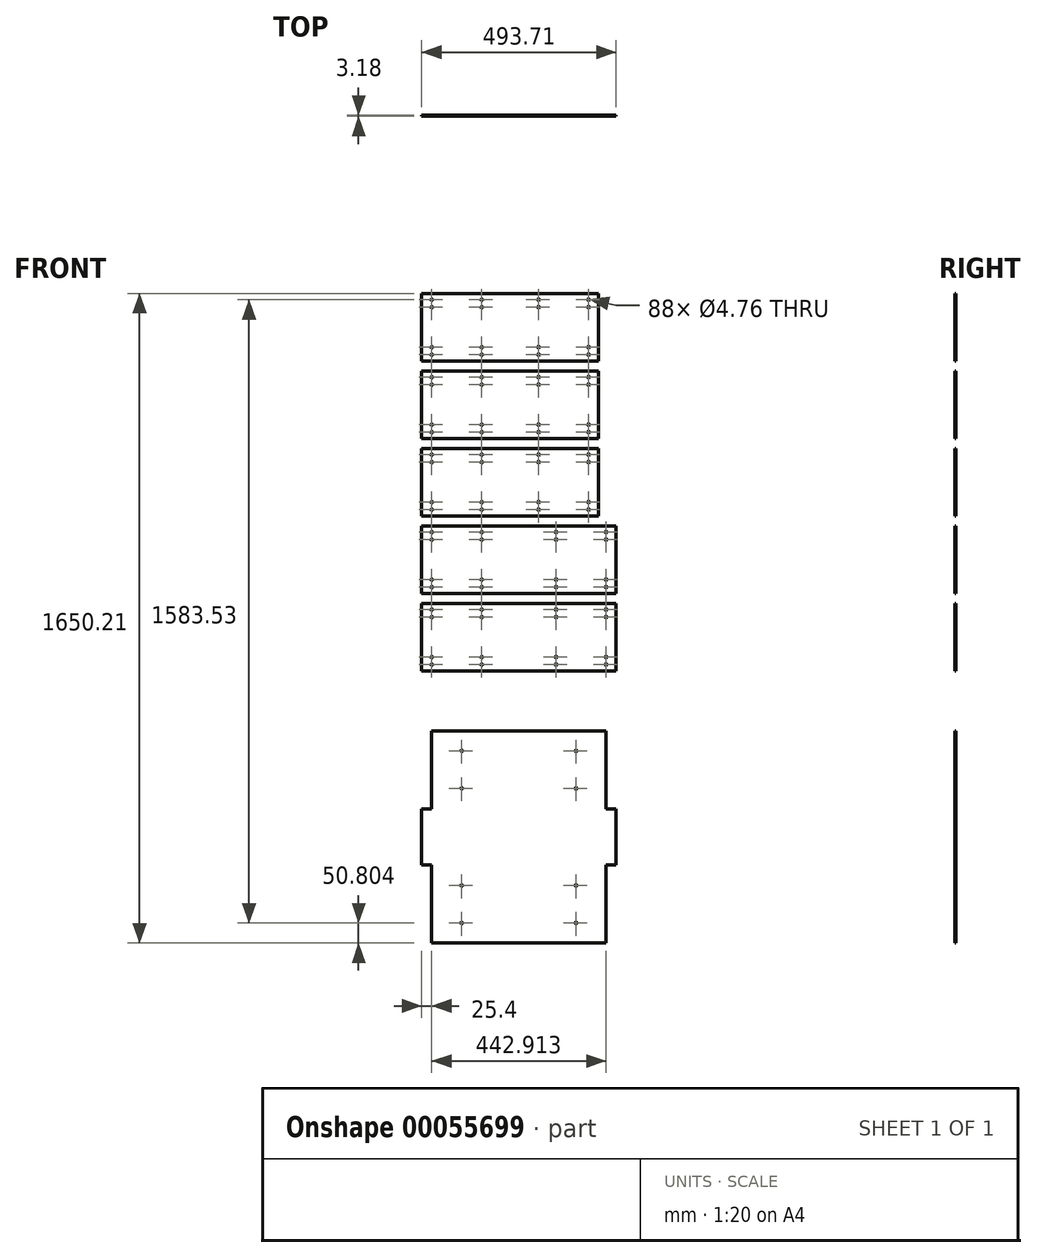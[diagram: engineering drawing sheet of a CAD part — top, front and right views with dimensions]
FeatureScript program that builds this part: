
annotation { "Feature Type Name" : "Feature", "Feature Type Description" : "" }
export const myFeature = defineFeature(function(context is Context, id is Id, definition is map)
    precondition{}
    {
        {
            var Q0;
            Q0=qCreatedBy(makeId("Front.planeOp"),FACE);
            var sketch = newSketch(context, id + "F0", { "sketchPlane" : qUnion([Q0])});
            skLineSegment(sketch, "E0", {"start": v(0, 0) * mm, "end": v(0, -2201.05) * mm, "construction": true});
            skLineSegment(sketch, "E1.bottom", {"start": v(0, 0) * mm, "end": v(449.26, 0) * mm});
            skLineSegment(sketch, "E1.top", {"start": v(0, -171.45) * mm, "end": v(449.26, -171.45) * mm});
            skLineSegment(sketch, "E1.left", {"start": v(0, 0) * mm, "end": v(0, -171.45) * mm});
            skLineSegment(sketch, "E1.right", {"start": v(449.26, 0) * mm, "end": v(449.26, -171.45) * mm});
            skLineSegment(sketch, "E2", {"start": v(0, -15.88) * mm, "end": v(449.26, -15.88) * mm, "construction": true});
            skLineSegment(sketch, "E3", {"start": v(0, -34.93) * mm, "end": v(449.26, -34.93) * mm, "construction": true});
            skLineSegment(sketch, "E4", {"start": v(0, -136.53) * mm, "end": v(449.26, -136.52) * mm, "construction": true});
            skLineSegment(sketch, "E5", {"start": v(0, -155.58) * mm, "end": v(449.26, -155.58) * mm, "construction": true});
            skCircle(sketch, "E6", {"center": v(25.4, -15.88) * mm, "radius": 2.38 * mm});
            skCircle(sketch, "E7", {"center": v(152.4, -15.88) * mm, "radius": 2.38 * mm});
            skCircle(sketch, "E8", {"center": v(296.86, -15.87) * mm, "radius": 2.38 * mm});
            skCircle(sketch, "E9", {"center": v(423.86, -15.87) * mm, "radius": 2.38 * mm});
            skCircle(sketch, "E10", {"center": v(25.4, -34.93) * mm, "radius": 2.38 * mm});
            skCircle(sketch, "E11", {"center": v(152.4, -34.93) * mm, "radius": 2.38 * mm});
            skCircle(sketch, "E12", {"center": v(296.86, -34.92) * mm, "radius": 2.38 * mm});
            skCircle(sketch, "E13", {"center": v(423.86, -34.92) * mm, "radius": 2.38 * mm});
            skCircle(sketch, "E14", {"center": v(25.4, -136.53) * mm, "radius": 2.38 * mm});
            skCircle(sketch, "E15", {"center": v(152.4, -136.53) * mm, "radius": 2.38 * mm});
            skCircle(sketch, "E16", {"center": v(296.86, -136.52) * mm, "radius": 2.38 * mm});
            skCircle(sketch, "E17", {"center": v(423.86, -136.52) * mm, "radius": 2.38 * mm});
            skCircle(sketch, "E18", {"center": v(25.4, -155.58) * mm, "radius": 2.38 * mm});
            skCircle(sketch, "E19", {"center": v(152.4, -155.58) * mm, "radius": 2.38 * mm});
            skCircle(sketch, "E20", {"center": v(296.86, -155.57) * mm, "radius": 2.38 * mm});
            skCircle(sketch, "E21", {"center": v(423.86, -155.57) * mm, "radius": 2.38 * mm});
            skLineSegment(sketch, "E22", {"start": v(25.4, -15.88) * mm, "end": v(25.4, -155.58) * mm, "construction": true});
            skLineSegment(sketch, "E23", {"start": v(152.4, -15.88) * mm, "end": v(152.4, -155.58) * mm, "construction": true});
            skLineSegment(sketch, "E24", {"start": v(296.86, -15.87) * mm, "end": v(296.86, -155.57) * mm, "construction": true});
            skLineSegment(sketch, "E25", {"start": v(423.86, -15.87) * mm, "end": v(423.86, -155.57) * mm, "construction": true});
            skLineSegment(sketch, "E26.bottom", {"start": v(0, -590.55) * mm, "end": v(493.71, -590.55) * mm});
            skLineSegment(sketch, "E26.top", {"start": v(0, -762) * mm, "end": v(493.71, -762) * mm});
            skLineSegment(sketch, "E26.left", {"start": v(0, -590.55) * mm, "end": v(0, -762) * mm});
            skLineSegment(sketch, "E26.right", {"start": v(493.71, -590.55) * mm, "end": v(493.71, -762) * mm});
            skLineSegment(sketch, "E27", {"start": v(0, -606.43) * mm, "end": v(493.71, -606.43) * mm, "construction": true});
            skLineSegment(sketch, "E28", {"start": v(0, -727.08) * mm, "end": v(493.71, -727.08) * mm, "construction": true});
            skLineSegment(sketch, "E29", {"start": v(0, -625.48) * mm, "end": v(493.71, -625.48) * mm, "construction": true});
            skLineSegment(sketch, "E30", {"start": v(0, -746.13) * mm, "end": v(493.71, -746.13) * mm, "construction": true});
            skLineSegment(sketch, "E31", {"start": v(25.4, -590.55) * mm, "end": v(25.4, -762) * mm, "construction": true});
            skLineSegment(sketch, "E32", {"start": v(152.4, -590.55) * mm, "end": v(152.4, -762) * mm, "construction": true});
            skLineSegment(sketch, "E33", {"start": v(341.31, -590.55) * mm, "end": v(341.31, -762) * mm, "construction": true});
            skLineSegment(sketch, "E34", {"start": v(468.31, -590.55) * mm, "end": v(468.31, -762) * mm, "construction": true});
            skCircle(sketch, "E35", {"center": v(25.4, -606.43) * mm, "radius": 2.38 * mm});
            skCircle(sketch, "E36", {"center": v(25.4, -625.48) * mm, "radius": 2.38 * mm});
            skCircle(sketch, "E37", {"center": v(152.4, -606.43) * mm, "radius": 2.38 * mm});
            skCircle(sketch, "E38", {"center": v(152.4, -625.48) * mm, "radius": 2.38 * mm});
            skCircle(sketch, "E39", {"center": v(341.31, -606.43) * mm, "radius": 2.38 * mm});
            skCircle(sketch, "E40", {"center": v(468.31, -606.43) * mm, "radius": 2.38 * mm});
            skCircle(sketch, "E41", {"center": v(468.31, -625.48) * mm, "radius": 2.38 * mm});
            skCircle(sketch, "E42", {"center": v(341.31, -625.48) * mm, "radius": 2.38 * mm});
            skCircle(sketch, "E43", {"center": v(25.4, -727.08) * mm, "radius": 2.38 * mm});
            skCircle(sketch, "E44", {"center": v(25.4, -746.13) * mm, "radius": 2.38 * mm});
            skCircle(sketch, "E45", {"center": v(152.4, -746.13) * mm, "radius": 2.38 * mm});
            skCircle(sketch, "E46", {"center": v(152.4, -727.08) * mm, "radius": 2.38 * mm});
            skCircle(sketch, "E47", {"center": v(341.31, -727.08) * mm, "radius": 2.38 * mm});
            skCircle(sketch, "E48", {"center": v(341.31, -746.13) * mm, "radius": 2.38 * mm});
            skCircle(sketch, "E49", {"center": v(468.31, -727.08) * mm, "radius": 2.38 * mm});
            skCircle(sketch, "E50", {"center": v(468.31, -746.13) * mm, "radius": 2.38 * mm});
            skLineSegment(sketch, "E51.bottom", {"start": v(0, -196.85) * mm, "end": v(449.26, -196.85) * mm});
            skLineSegment(sketch, "E51.top", {"start": v(0, -368.3) * mm, "end": v(449.26, -368.3) * mm});
            skLineSegment(sketch, "E51.left", {"start": v(0, -196.85) * mm, "end": v(0, -368.3) * mm});
            skLineSegment(sketch, "E51.right", {"start": v(449.26, -196.85) * mm, "end": v(449.26, -368.3) * mm});
            skLineSegment(sketch, "E52", {"start": v(0, -212.73) * mm, "end": v(449.26, -212.72) * mm, "construction": true});
            skLineSegment(sketch, "E53", {"start": v(0, -231.78) * mm, "end": v(449.26, -231.77) * mm, "construction": true});
            skLineSegment(sketch, "E54", {"start": v(0, -333.38) * mm, "end": v(449.26, -333.37) * mm, "construction": true});
            skLineSegment(sketch, "E55", {"start": v(0, -352.43) * mm, "end": v(449.26, -352.43) * mm, "construction": true});
            skCircle(sketch, "E56", {"center": v(25.4, -212.73) * mm, "radius": 2.38 * mm});
            skCircle(sketch, "E57", {"center": v(152.4, -212.73) * mm, "radius": 2.38 * mm});
            skCircle(sketch, "E58", {"center": v(296.86, -212.72) * mm, "radius": 2.38 * mm});
            skCircle(sketch, "E59", {"center": v(423.86, -212.72) * mm, "radius": 2.38 * mm});
            skCircle(sketch, "E60", {"center": v(25.4, -231.78) * mm, "radius": 2.38 * mm});
            skCircle(sketch, "E61", {"center": v(152.4, -231.78) * mm, "radius": 2.38 * mm});
            skCircle(sketch, "E62", {"center": v(296.86, -231.77) * mm, "radius": 2.38 * mm});
            skCircle(sketch, "E63", {"center": v(423.86, -231.77) * mm, "radius": 2.38 * mm});
            skCircle(sketch, "E64", {"center": v(25.4, -333.38) * mm, "radius": 2.38 * mm});
            skCircle(sketch, "E65", {"center": v(152.4, -333.38) * mm, "radius": 2.38 * mm});
            skCircle(sketch, "E66", {"center": v(296.86, -333.38) * mm, "radius": 2.38 * mm});
            skCircle(sketch, "E67", {"center": v(423.86, -333.37) * mm, "radius": 2.38 * mm});
            skCircle(sketch, "E68", {"center": v(25.4, -352.43) * mm, "radius": 2.38 * mm});
            skCircle(sketch, "E69", {"center": v(152.4, -352.43) * mm, "radius": 2.38 * mm});
            skCircle(sketch, "E70", {"center": v(296.86, -352.43) * mm, "radius": 2.38 * mm});
            skCircle(sketch, "E71", {"center": v(423.86, -352.43) * mm, "radius": 2.38 * mm});
            skLineSegment(sketch, "E72", {"start": v(25.4, -212.73) * mm, "end": v(25.4, -352.43) * mm, "construction": true});
            skLineSegment(sketch, "E73", {"start": v(152.4, -212.73) * mm, "end": v(152.4, -352.43) * mm, "construction": true});
            skLineSegment(sketch, "E74", {"start": v(296.86, -212.72) * mm, "end": v(296.86, -352.43) * mm, "construction": true});
            skLineSegment(sketch, "E75", {"start": v(423.86, -212.72) * mm, "end": v(423.86, -352.43) * mm, "construction": true});
            skLineSegment(sketch, "E76.bottom", {"start": v(0, -393.7) * mm, "end": v(449.26, -393.7) * mm});
            skLineSegment(sketch, "E76.top", {"start": v(0, -565.15) * mm, "end": v(449.26, -565.15) * mm});
            skLineSegment(sketch, "E76.left", {"start": v(0, -393.7) * mm, "end": v(0, -565.15) * mm});
            skLineSegment(sketch, "E76.right", {"start": v(449.26, -393.7) * mm, "end": v(449.26, -565.15) * mm});
            skLineSegment(sketch, "E77", {"start": v(0, -409.58) * mm, "end": v(449.26, -409.57) * mm, "construction": true});
            skLineSegment(sketch, "E78", {"start": v(0, -428.63) * mm, "end": v(449.26, -428.62) * mm, "construction": true});
            skLineSegment(sketch, "E79", {"start": v(0, -530.23) * mm, "end": v(449.26, -530.22) * mm, "construction": true});
            skLineSegment(sketch, "E80", {"start": v(0, -549.28) * mm, "end": v(449.26, -549.28) * mm, "construction": true});
            skCircle(sketch, "E81", {"center": v(25.4, -409.58) * mm, "radius": 2.38 * mm});
            skCircle(sketch, "E82", {"center": v(152.4, -409.58) * mm, "radius": 2.38 * mm});
            skCircle(sketch, "E83", {"center": v(296.86, -409.58) * mm, "radius": 2.38 * mm});
            skCircle(sketch, "E84", {"center": v(423.86, -409.57) * mm, "radius": 2.38 * mm});
            skCircle(sketch, "E85", {"center": v(25.4, -428.63) * mm, "radius": 2.38 * mm});
            skCircle(sketch, "E86", {"center": v(152.4, -428.63) * mm, "radius": 2.38 * mm});
            skCircle(sketch, "E87", {"center": v(296.86, -428.63) * mm, "radius": 2.38 * mm});
            skCircle(sketch, "E88", {"center": v(423.86, -428.62) * mm, "radius": 2.38 * mm});
            skCircle(sketch, "E89", {"center": v(25.4, -530.23) * mm, "radius": 2.38 * mm});
            skCircle(sketch, "E90", {"center": v(152.4, -530.23) * mm, "radius": 2.38 * mm});
            skCircle(sketch, "E91", {"center": v(296.86, -530.23) * mm, "radius": 2.38 * mm});
            skCircle(sketch, "E92", {"center": v(423.86, -530.22) * mm, "radius": 2.38 * mm});
            skCircle(sketch, "E93", {"center": v(25.4, -549.28) * mm, "radius": 2.38 * mm});
            skCircle(sketch, "E94", {"center": v(152.4, -549.28) * mm, "radius": 2.38 * mm});
            skCircle(sketch, "E95", {"center": v(296.86, -549.28) * mm, "radius": 2.38 * mm});
            skCircle(sketch, "E96", {"center": v(423.86, -549.28) * mm, "radius": 2.38 * mm});
            skLineSegment(sketch, "E97", {"start": v(25.4, -409.58) * mm, "end": v(25.4, -549.28) * mm, "construction": true});
            skLineSegment(sketch, "E98", {"start": v(152.4, -409.58) * mm, "end": v(152.4, -549.28) * mm, "construction": true});
            skLineSegment(sketch, "E99", {"start": v(296.86, -409.58) * mm, "end": v(296.86, -549.28) * mm, "construction": true});
            skLineSegment(sketch, "E100", {"start": v(423.86, -409.57) * mm, "end": v(423.86, -549.28) * mm, "construction": true});
            skLineSegment(sketch, "E101.bottom", {"start": v(0, -787.4) * mm, "end": v(493.71, -787.4) * mm});
            skLineSegment(sketch, "E101.top", {"start": v(0, -958.85) * mm, "end": v(493.71, -958.85) * mm});
            skLineSegment(sketch, "E101.left", {"start": v(0, -787.4) * mm, "end": v(0, -958.85) * mm});
            skLineSegment(sketch, "E101.right", {"start": v(493.71, -787.4) * mm, "end": v(493.71, -958.85) * mm});
            skLineSegment(sketch, "E102", {"start": v(0, -803.28) * mm, "end": v(493.71, -803.28) * mm, "construction": true});
            skLineSegment(sketch, "E103", {"start": v(0, -923.93) * mm, "end": v(493.71, -923.92) * mm, "construction": true});
            skLineSegment(sketch, "E104", {"start": v(0, -822.33) * mm, "end": v(493.71, -822.33) * mm, "construction": true});
            skLineSegment(sketch, "E105", {"start": v(0, -942.98) * mm, "end": v(493.71, -942.98) * mm, "construction": true});
            skLineSegment(sketch, "E106", {"start": v(25.4, -787.4) * mm, "end": v(25.4, -958.85) * mm, "construction": true});
            skLineSegment(sketch, "E107", {"start": v(152.4, -787.4) * mm, "end": v(152.4, -958.85) * mm, "construction": true});
            skLineSegment(sketch, "E108", {"start": v(341.31, -787.4) * mm, "end": v(341.31, -958.85) * mm, "construction": true});
            skLineSegment(sketch, "E109", {"start": v(468.31, -787.4) * mm, "end": v(468.31, -958.85) * mm, "construction": true});
            skCircle(sketch, "E110", {"center": v(25.4, -803.28) * mm, "radius": 2.38 * mm});
            skCircle(sketch, "E111", {"center": v(25.4, -822.33) * mm, "radius": 2.38 * mm});
            skCircle(sketch, "E112", {"center": v(152.4, -803.28) * mm, "radius": 2.38 * mm});
            skCircle(sketch, "E113", {"center": v(152.4, -822.33) * mm, "radius": 2.38 * mm});
            skCircle(sketch, "E114", {"center": v(468.31, -822.33) * mm, "radius": 2.38 * mm});
            skCircle(sketch, "E115", {"center": v(152.4, -942.98) * mm, "radius": 2.38 * mm});
            skCircle(sketch, "E116", {"center": v(152.4, -923.93) * mm, "radius": 2.38 * mm});
            skCircle(sketch, "E117", {"center": v(341.31, -942.98) * mm, "radius": 2.38 * mm});
            skCircle(sketch, "E118", {"center": v(468.31, -923.92) * mm, "radius": 2.38 * mm});
            skLineSegment(sketch, "E119", {"start": v(0, -1309.69) * mm, "end": v(25.4, -1309.69) * mm});
            skLineSegment(sketch, "E120", {"start": v(25.4, -1309.69) * mm, "end": v(25.4, -1111.25) * mm});
            skLineSegment(sketch, "E121", {"start": v(25.4, -1111.25) * mm, "end": v(468.31, -1111.25) * mm});
            skLineSegment(sketch, "E122", {"start": v(468.31, -1111.25) * mm, "end": v(468.31, -1309.69) * mm});
            skLineSegment(sketch, "E123", {"start": v(468.31, -1309.69) * mm, "end": v(493.71, -1309.69) * mm});
            skLineSegment(sketch, "E124", {"start": v(493.71, -1309.69) * mm, "end": v(493.71, -1451.77) * mm});
            skLineSegment(sketch, "E125", {"start": v(493.71, -1451.77) * mm, "end": v(468.31, -1451.77) * mm});
            skLineSegment(sketch, "E126", {"start": v(468.31, -1451.77) * mm, "end": v(468.31, -1650.2) * mm});
            skLineSegment(sketch, "E127", {"start": v(468.31, -1650.2) * mm, "end": v(25.4, -1650.2) * mm});
            skLineSegment(sketch, "E128", {"start": v(25.4, -1650.2) * mm, "end": v(25.4, -1451.77) * mm});
            skLineSegment(sketch, "E129", {"start": v(25.4, -1451.77) * mm, "end": v(0, -1451.77) * mm});
            skLineSegment(sketch, "E130", {"start": v(0, -1451.77) * mm, "end": v(0, -1309.69) * mm});
            skLineSegment(sketch, "E131", {"start": v(101.6, -1111.25) * mm, "end": v(101.6, -1650.2) * mm, "construction": true});
            skLineSegment(sketch, "E132", {"start": v(392.11, -1111.25) * mm, "end": v(392.11, -1650.2) * mm, "construction": true});
            skLineSegment(sketch, "E133", {"start": v(25.4, -1162.05) * mm, "end": v(468.31, -1162.05) * mm, "construction": true});
            skLineSegment(sketch, "E134", {"start": v(25.4, -1257.3) * mm, "end": v(468.31, -1257.3) * mm, "construction": true});
            skLineSegment(sketch, "E135", {"start": v(25.4, -1504.16) * mm, "end": v(468.31, -1504.16) * mm, "construction": true});
            skLineSegment(sketch, "E136", {"start": v(25.4, -1599.4) * mm, "end": v(468.31, -1599.4) * mm, "construction": true});
            skCircle(sketch, "E137", {"center": v(101.6, -1162.05) * mm, "radius": 2.38 * mm});
            skCircle(sketch, "E138", {"center": v(392.11, -1162.05) * mm, "radius": 2.38 * mm});
            skCircle(sketch, "E139", {"center": v(392.11, -1257.3) * mm, "radius": 2.38 * mm});
            skCircle(sketch, "E140", {"center": v(101.6, -1257.3) * mm, "radius": 2.38 * mm});
            skCircle(sketch, "E141", {"center": v(101.6, -1504.16) * mm, "radius": 2.38 * mm});
            skCircle(sketch, "E142", {"center": v(101.6, -1599.4) * mm, "radius": 2.38 * mm});
            skCircle(sketch, "E143", {"center": v(392.11, -1504.16) * mm, "radius": 2.38 * mm});
            skCircle(sketch, "E144", {"center": v(392.11, -1599.4) * mm, "radius": 2.38 * mm});
            skCircle(sketch, "E145", {"center": v(341.31, -803.28) * mm, "radius": 2.38 * mm});
            skCircle(sketch, "E146", {"center": v(341.31, -822.33) * mm, "radius": 2.38 * mm});
            skCircle(sketch, "E147", {"center": v(341.31, -923.92) * mm, "radius": 2.38 * mm});
            skCircle(sketch, "E148", {"center": v(468.31, -803.28) * mm, "radius": 2.38 * mm});
            skCircle(sketch, "E149", {"center": v(25.4, -923.93) * mm, "radius": 2.38 * mm});
            skCircle(sketch, "E150", {"center": v(25.4, -942.98) * mm, "radius": 2.38 * mm});
            skCircle(sketch, "E151", {"center": v(468.31, -942.98) * mm, "radius": 2.38 * mm});
            skSolve(sketch);
        }
        {
            var Q0;
            Q0 = qSketchRegion(id + "F0", true);
            extrude(context, id + "F1", {"entities" : qUnion([Q0]), "depth" : 3.17 * mm});
        }
    });
